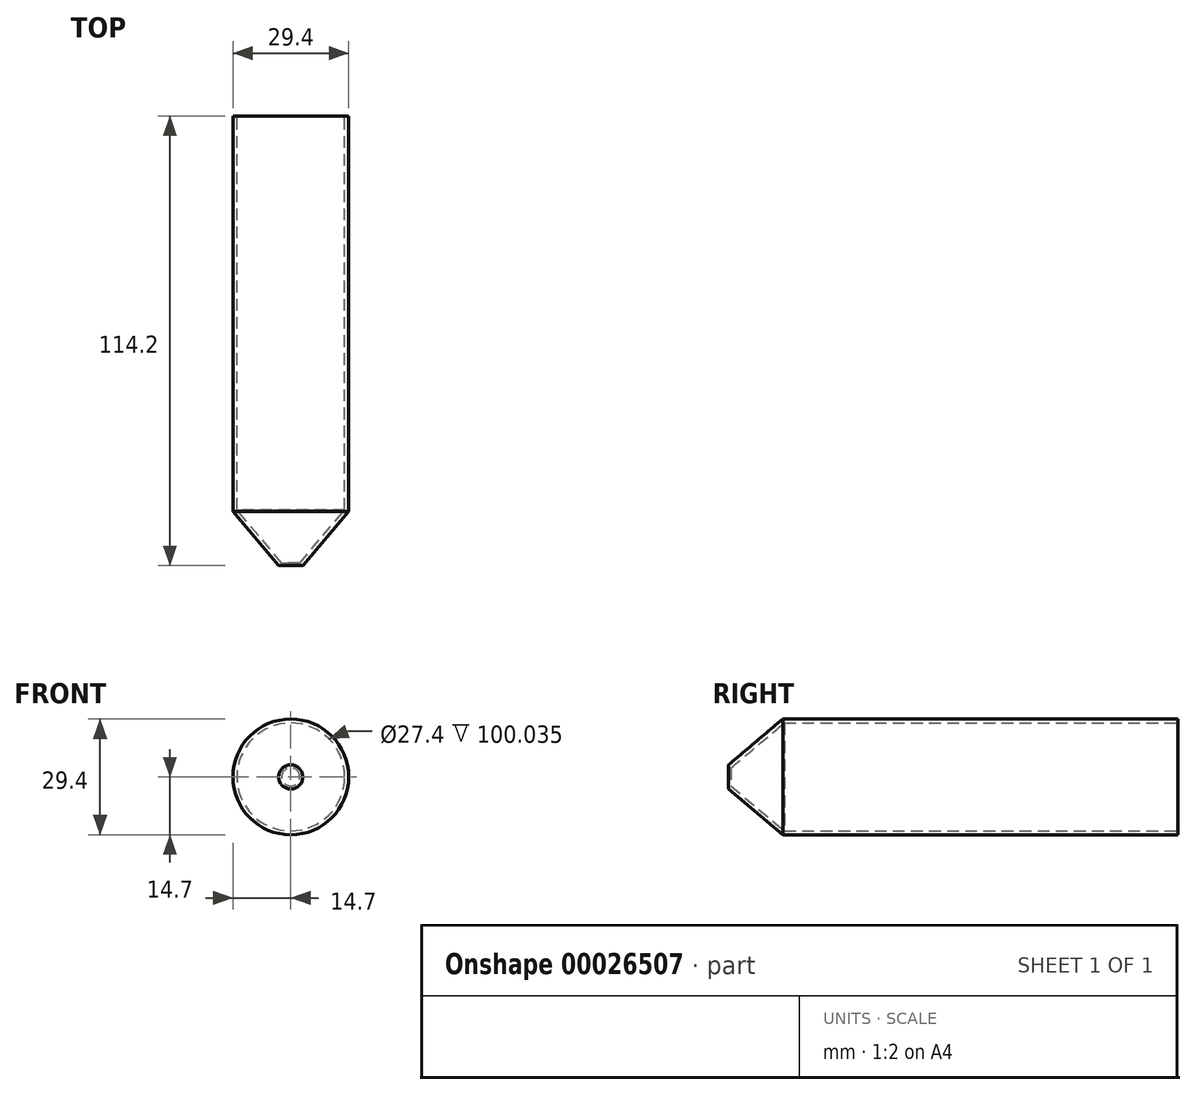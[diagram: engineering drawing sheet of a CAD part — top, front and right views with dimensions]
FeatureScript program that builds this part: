
annotation { "Feature Type Name" : "Feature", "Feature Type Description" : "" }
export const myFeature = defineFeature(function(context is Context, id is Id, definition is map)
    precondition{}
    {
        {
            var Q0;
            Q0=qCreatedBy(makeId("Top.planeOp"),FACE);
            var sketch = newSketch(context, id + "F0", { "sketchPlane" : qUnion([Q0])});
            skLineSegment(sketch, "E0", {"start": v(0, 0) * mm, "end": v(3.07, 0) * mm});
            skLineSegment(sketch, "E1", {"start": v(3.07, 0) * mm, "end": v(14.7, 13.8) * mm});
            skLineSegment(sketch, "E2", {"start": v(14.7, 13.8) * mm, "end": v(14.7, 114.2) * mm});
            skPoint(sketch, "E3.end.orphan", {"position": v(0, 114.2) * mm});
            skLineSegment(sketch, "E4", {"start": v(14.7, 114.2) * mm, "end": v(14.7, 13.8) * mm});
            skLineSegment(sketch, "E5", {"start": v(0, 114.2) * mm, "end": v(0, 0) * mm, "construction": true});
            skLineSegment(sketch, "E6", {"start": v(0, 114.2) * mm, "end": v(14.7, 114.2) * mm});
            skPoint(sketch, "E7.orphan", {"position": v(14.7, 0) * mm});
            skLineSegment(sketch, "E8.0", {"start": v(13.7, 114.2) * mm, "end": v(13.7, 14.17) * mm});
            skLineSegment(sketch, "E8.1", {"start": v(2.3, 0.64) * mm, "end": v(13.7, 14.17) * mm});
            skLineSegment(sketch, "E9", {"start": v(2.3, 0.64) * mm, "end": v(0, 0.64) * mm});
            skLineSegment(sketch, "E10", {"start": v(0, 0.64) * mm, "end": v(0, 0) * mm});
            skSolve(sketch);
        }
        {
            var Q0;
            Q0=makeQuery(id+"F0.imprint","IMPRINT",FACE,{"disambiguationData":[TD([[makeQuery(id+"F0.imprint","IMPRINT",EDGE,{"derivedFrom":sQuery(id+"F0.wireOp",EDGE,"E0")}),1.0]])]});
            var Q1;
            Q1=sQuery(id+"F0.wireOp",EDGE,"E5");
            revolve(context, id + "F1", {"entities" : qUnion([Q0]), "axis" : qUnion([Q1]), "revolveType" : RevolveType.FULL});
        }
    });
